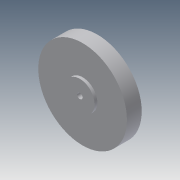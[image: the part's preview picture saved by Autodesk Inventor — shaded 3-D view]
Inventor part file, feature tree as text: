
AUTODESK INVENTOR PART (.ipt)
format: ipt  version: 2014 (Build 180170000, 170)  size: 89,088 bytes
history: native  units: in
note: dims shown in document units (in); Inventor stores cm internally (conversion verified against a paired STEP export)
features: extrude x3, sketch x3
ambient origin geometry x8: Origin, YZ Plane, XZ Plane, XY Plane, X Axis, Y Axis, Z Axis, Center Point
bodies: Solid1 (feature_tree)
feature tree (6):
  extrude  "Extrusion1"  Depth=1.0in TaperAngle=0.0deg
  extrude  "Extrusion2"  Depth=0.1875in TaperAngle=0.0deg
  extrude  "Extrusion3"  Depth=1.375in TaperAngle=0.0deg
  sketch  "Sketch1"  dims[d0=6.0in d1=1.0in d2=0.0in]
  sketch  "Sketch2"  dims[d3=2.0in d4=0.1875in d5=1.1875in d6=0.0in d7=0.0in]
  sketch  "Sketch3"  dims[d8=0.375in d9=1.375in d10=0.0in]
